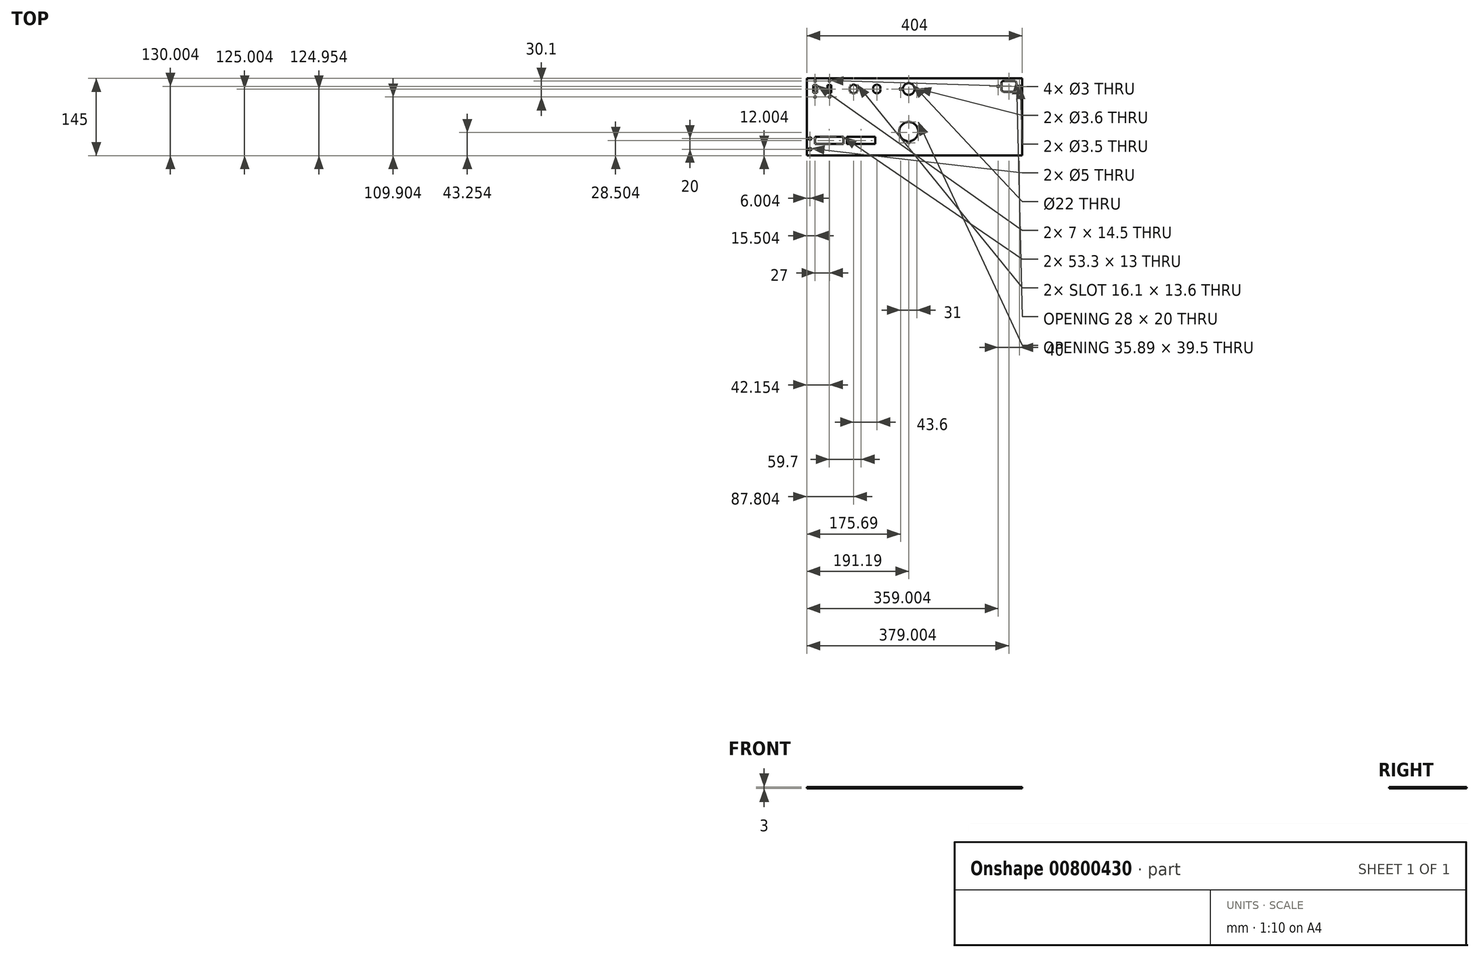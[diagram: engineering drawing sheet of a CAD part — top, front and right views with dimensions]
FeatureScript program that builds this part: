
annotation { "Feature Type Name" : "Feature", "Feature Type Description" : "" }
export const myFeature = defineFeature(function(context is Context, id is Id, definition is map)
    precondition{}
    {
        {
            var Q0;
            Q0=qCreatedBy(makeId("Top.planeOp"),FACE);
            var sketch = newSketch(context, id + "F0", { "sketchPlane" : qUnion([Q0])});
            skLineSegment(sketch, "E0.bottom", {"start": v(-216.19, 64.87) * mm, "end": v(187.81, 64.87) * mm});
            skLineSegment(sketch, "E0.top", {"start": v(-216.19, -80.13) * mm, "end": v(187.81, -80.13) * mm});
            skLineSegment(sketch, "E0.left", {"start": v(-216.19, 64.87) * mm, "end": v(-216.19, -80.13) * mm});
            skLineSegment(sketch, "E0.right", {"start": v(187.81, 64.87) * mm, "end": v(187.81, -80.13) * mm});
            skSolve(sketch);
        }
        {
            var Q0;
            Q0=qCreatedBy(makeId("Top.planeOp"),FACE);
            var sketch = newSketch(context, id + "F1", { "sketchPlane" : qUnion([Q0])});
            skCircle(sketch, "E1", {"center": v(-210.19, -68.13) * mm, "radius": 2.5 * mm});
            skArc(sketch, "E2", {"start": v(-135.19, 40.57) * mm, "mid": v(-128.39, 36.82) * mm, "end": v(-121.59, 40.57) * mm});
            skLineSegment(sketch, "E3", {"start": v(-135.19, 49.18) * mm, "end": v(-135.19, 40.57) * mm});
            skLineSegment(sketch, "E4", {"start": v(-121.59, 49.18) * mm, "end": v(-121.59, 40.57) * mm});
            skArc(sketch, "E5.trimOffspring", {"start": v(-121.59, 49.18) * mm, "mid": v(-128.39, 52.92) * mm, "end": v(-135.19, 49.18) * mm});
            skCircle(sketch, "E6", {"center": v(-25, -35.13) * mm, "radius": 18 * mm});
            skLineSegment(sketch, "E7.bottom", {"start": v(-27.75, -56.63) * mm, "end": v(-22.25, -56.63) * mm});
            skLineSegment(sketch, "E7.top", {"start": v(-27.75, -31.4) * mm, "end": v(-22.25, -31.4) * mm});
            skLineSegment(sketch, "E7.left", {"start": v(-27.75, -56.63) * mm, "end": v(-27.75, -31.4) * mm});
            skLineSegment(sketch, "E7.right", {"start": v(-22.25, -56.63) * mm, "end": v(-22.25, -31.4) * mm});
            skCircle(sketch, "E8", {"center": v(-25, 44.87) * mm, "radius": 11 * mm});
            skCircle(sketch, "E9", {"center": v(-40.5, 44.87) * mm, "radius": 1.8 * mm});
            skCircle(sketch, "E10.MirrorC", {"center": v(-9.5, 44.87) * mm, "radius": 1.8 * mm});
            skCircle(sketch, "E11.0.1.0", {"center": v(-210.19, -48.13) * mm, "radius": 2.5 * mm});
            skLineSegment(sketch, "E11.direction1", {"start": v(-210.19, -68.13) * mm, "end": v(-163.19, -68.13) * mm, "construction": true});
            skLineSegment(sketch, "E11.direction2", {"start": v(-210.19, -68.13) * mm, "end": v(-210.19, -48.13) * mm, "construction": true});
            skLineSegment(sketch, "E12.bottom", {"start": v(172.81, 39.87) * mm, "end": v(152.81, 39.87) * mm});
            skLineSegment(sketch, "E12.top", {"start": v(172.81, 59.87) * mm, "end": v(152.81, 59.87) * mm});
            skLineSegment(sketch, "E12.left", {"start": v(176.81, 43.87) * mm, "end": v(176.81, 55.87) * mm});
            skLineSegment(sketch, "E12.right", {"start": v(148.81, 43.87) * mm, "end": v(148.81, 55.87) * mm});
            skPoint(sketch, "E12.middle", {"position": v(162.81, 49.87) * mm});
            skCircle(sketch, "E13", {"center": v(142.81, 49.87) * mm, "radius": 1.75 * mm});
            skCircle(sketch, "E14", {"center": v(182.81, 49.87) * mm, "radius": 1.75 * mm});
            skPoint(sketch, "E15.visualSharp", {"position": v(148.81, 59.87) * mm});
            skArc(sketch, "E15.filletArc", {"start": v(152.81, 59.87) * mm, "mid": v(149.99, 58.7) * mm, "end": v(148.81, 55.87) * mm});
            skPoint(sketch, "E16.visualSharp", {"position": v(176.81, 59.87) * mm});
            skArc(sketch, "E16.filletArc", {"start": v(176.81, 55.87) * mm, "mid": v(175.64, 58.7) * mm, "end": v(172.81, 59.87) * mm});
            skPoint(sketch, "E17.visualSharp", {"position": v(176.81, 39.87) * mm});
            skArc(sketch, "E17.filletArc", {"start": v(172.81, 39.87) * mm, "mid": v(175.64, 41.05) * mm, "end": v(176.81, 43.87) * mm});
            skPoint(sketch, "E18.visualSharp", {"position": v(148.81, 39.87) * mm});
            skArc(sketch, "E18.filletArc", {"start": v(148.81, 43.87) * mm, "mid": v(149.99, 41.05) * mm, "end": v(152.81, 39.87) * mm});
            skLineSegment(sketch, "E19.bottom", {"start": v(-204.19, 11.87) * mm, "end": v(-84.19, 11.87) * mm, "construction": true});
            skLineSegment(sketch, "E19.top", {"start": v(-204.19, -68.13) * mm, "end": v(-84.19, -68.13) * mm, "construction": true});
            skLineSegment(sketch, "E19.left", {"start": v(-204.19, 11.87) * mm, "end": v(-204.19, -68.13) * mm, "construction": true});
            skLineSegment(sketch, "E19.right", {"start": v(-84.19, 11.87) * mm, "end": v(-84.19, -68.13) * mm, "construction": true});
            skLineSegment(sketch, "E20.bottom", {"start": v(-147.39, -45.13) * mm, "end": v(-200.69, -45.13) * mm});
            skLineSegment(sketch, "E20.top", {"start": v(-147.39, -58.13) * mm, "end": v(-200.69, -58.13) * mm});
            skLineSegment(sketch, "E20.left", {"start": v(-147.39, -45.13) * mm, "end": v(-147.39, -58.13) * mm});
            skLineSegment(sketch, "E20.right", {"start": v(-200.69, -45.13) * mm, "end": v(-200.69, -58.13) * mm});
            skPoint(sketch, "E20.middle", {"position": v(-174.04, -51.63) * mm});
            skLineSegment(sketch, "E21.bottom", {"start": v(-87.69, -45.13) * mm, "end": v(-140.99, -45.13) * mm});
            skLineSegment(sketch, "E21.top", {"start": v(-87.69, -58.13) * mm, "end": v(-140.99, -58.13) * mm});
            skLineSegment(sketch, "E21.left", {"start": v(-87.69, -45.13) * mm, "end": v(-87.69, -58.13) * mm});
            skLineSegment(sketch, "E21.right", {"start": v(-140.99, -45.13) * mm, "end": v(-140.99, -58.13) * mm});
            skPoint(sketch, "E21.middle", {"position": v(-114.34, -51.63) * mm});
            skLineSegment(sketch, "E22.bottom", {"start": v(-197.19, 37.57) * mm, "end": v(-204.19, 37.57) * mm});
            skLineSegment(sketch, "E22.top", {"start": v(-197.19, 52.07) * mm, "end": v(-204.19, 52.07) * mm});
            skLineSegment(sketch, "E22.left", {"start": v(-197.19, 37.57) * mm, "end": v(-197.19, 52.07) * mm});
            skLineSegment(sketch, "E22.right", {"start": v(-204.19, 37.57) * mm, "end": v(-204.19, 52.07) * mm});
            skPoint(sketch, "E22.middle", {"position": v(-200.69, 44.82) * mm});
            skCircle(sketch, "E23", {"center": v(-200.69, 59.87) * mm, "radius": 1.5 * mm});
            skCircle(sketch, "E24", {"center": v(-200.69, 29.77) * mm, "radius": 1.5 * mm});
            skLineSegment(sketch, "E25.bottom", {"start": v(-170.19, 37.57) * mm, "end": v(-177.19, 37.57) * mm});
            skLineSegment(sketch, "E25.top", {"start": v(-170.19, 52.07) * mm, "end": v(-177.19, 52.07) * mm});
            skLineSegment(sketch, "E25.left", {"start": v(-170.19, 37.57) * mm, "end": v(-170.19, 52.07) * mm});
            skLineSegment(sketch, "E25.right", {"start": v(-177.19, 37.57) * mm, "end": v(-177.19, 52.07) * mm});
            skPoint(sketch, "E25.middle", {"position": v(-173.69, 44.82) * mm});
            skCircle(sketch, "E26", {"center": v(-173.69, 59.87) * mm, "radius": 1.5 * mm});
            skCircle(sketch, "E27", {"center": v(-173.69, 29.77) * mm, "radius": 1.5 * mm});
            skArc(sketch, "E28", {"start": v(-91.59, 40.57) * mm, "mid": v(-84.79, 36.82) * mm, "end": v(-77.99, 40.57) * mm});
            skLineSegment(sketch, "E29", {"start": v(-91.59, 49.18) * mm, "end": v(-91.59, 40.57) * mm});
            skLineSegment(sketch, "E30", {"start": v(-77.99, 49.18) * mm, "end": v(-77.99, 40.57) * mm});
            skArc(sketch, "E31.trimOffspring", {"start": v(-77.99, 49.18) * mm, "mid": v(-84.79, 52.92) * mm, "end": v(-91.59, 49.18) * mm});
            skLineSegment(sketch, "E32.bottom", {"start": v(12.81, 29.87) * mm, "end": v(182.81, 29.87) * mm, "construction": true});
            skLineSegment(sketch, "E32.top", {"start": v(12.81, -80.13) * mm, "end": v(182.81, -80.13) * mm, "construction": true});
            skLineSegment(sketch, "E32.left", {"start": v(12.81, 29.87) * mm, "end": v(12.81, -80.13) * mm, "construction": true});
            skLineSegment(sketch, "E32.right", {"start": v(182.81, 29.87) * mm, "end": v(182.81, -80.13) * mm, "construction": true});
            skSolve(sketch);
        }
        {
            var Q0;
            Q0=makeQuery(id+"F0.imprint","IMPRINT",FACE,{"disambiguationData":[TD([[makeQuery(id+"F0.imprint","IMPRINT",EDGE,{"derivedFrom":sQuery(id+"F0.wireOp",EDGE,"E0.bottom")}),-1.0]])]});
            extrude(context, id + "F2", {"entities" : qUnion([Q0]), "oppositeDirection" : true, "depth" : 3 * mm, "offsetDistance" : 25 * mm});
        }
        {
            var Q0;
            Q0=qSketchRegion(id+"F1",true);
            extrude(context, id + "F3", {"entities" : qUnion([Q0]), "operationType" : NewBodyOperationType.REMOVE, "oppositeDirection" : true, "depth" : 25 * mm, "offsetDistance" : 25 * mm});
        }
    });
